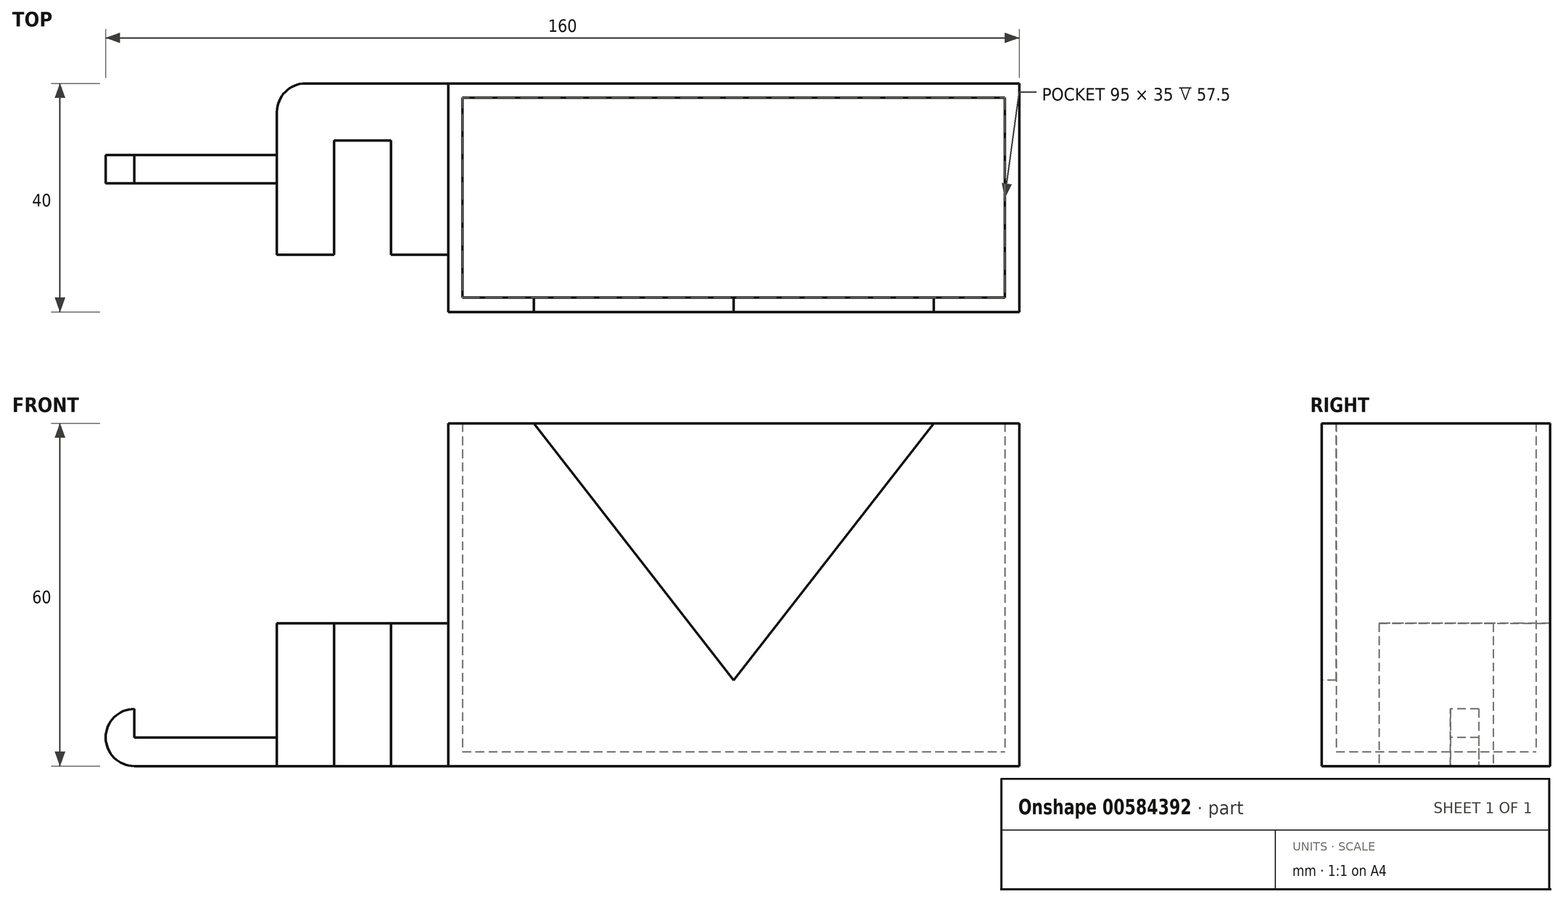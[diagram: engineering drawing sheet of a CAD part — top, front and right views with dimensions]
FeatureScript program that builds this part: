
annotation { "Feature Type Name" : "Feature", "Feature Type Description" : "" }
export const myFeature = defineFeature(function(context is Context, id is Id, definition is map)
    precondition{}
    {
        {
            var Q0;
            Q0=qCreatedBy(makeId("Top.planeOp"),FACE);
            var sketch = newSketch(context, id + "F0", { "sketchPlane" : qUnion([Q0])});
            skLineSegment(sketch, "E0.bottom", {"start": v(0, 0) * mm, "end": v(100, 0) * mm});
            skLineSegment(sketch, "E0.top", {"start": v(0, 40) * mm, "end": v(100, 40) * mm});
            skLineSegment(sketch, "E0.left", {"start": v(0, 0) * mm, "end": v(0, 40) * mm});
            skLineSegment(sketch, "E0.right", {"start": v(100, 0) * mm, "end": v(100, 40) * mm});
            skLineSegment(sketch, "E1", {"start": v(0, 40) * mm, "end": v(-30, 40) * mm});
            skLineSegment(sketch, "E2", {"start": v(-30, 40) * mm, "end": v(-30, 10) * mm});
            skLineSegment(sketch, "E3", {"start": v(-30, 10) * mm, "end": v(0, 10) * mm});
            skLineSegment(sketch, "E4", {"start": v(-30, 40) * mm, "end": v(-60, 40) * mm});
            skLineSegment(sketch, "E5", {"start": v(-60, 40) * mm, "end": v(-60, 10) * mm});
            skLineSegment(sketch, "E6", {"start": v(-60, 10) * mm, "end": v(-30, 10) * mm});
            skLineSegment(sketch, "E7", {"start": v(-10, 10) * mm, "end": v(-10, 30) * mm});
            skLineSegment(sketch, "E8", {"start": v(-10, 30) * mm, "end": v(-20, 30) * mm});
            skLineSegment(sketch, "E9", {"start": v(-20, 30) * mm, "end": v(-20, 10) * mm});
            skLineSegment(sketch, "E10", {"start": v(-40, 10) * mm, "end": v(-40, 30) * mm});
            skLineSegment(sketch, "E11", {"start": v(-40, 30) * mm, "end": v(-50, 30) * mm});
            skLineSegment(sketch, "E12", {"start": v(-50, 30) * mm, "end": v(-50, 10) * mm});
            skSolve(sketch);
        }
        {
            var Q0;
            Q0=makeQuery(id+"F0.imprint","IMPRINT",FACE,{"disambiguationData":[TD([[makeQuery(id+"F0.imprint","IMPRINT",EDGE,{"derivedFrom":sQuery(id+"F0.wireOp",EDGE,"E0.bottom")}),1.0]])]});
            extrude(context, id + "F1", {"entities" : qUnion([Q0]), "depth" : 60 * mm, "offsetDistance" : 25 * mm});
        }
        {
            var Q0;
            Q0=makeQuery(id+"F1.opExtrude","CAP_FACE",FACE,{"disambiguationData":[OSD([sQuery(id+"F0.wireOp",EDGE,"E0.bottom"),sQuery(id+"F0.wireOp",EDGE,"E0.top"),sQuery(id+"F0.wireOp",EDGE,"E0.right"),sQuery(id+"F0.wireOp",EDGE,"3OmhZuot-nZRl-fitB-kn2A-HAzrbiBYZeYS.left")])],"isStart":false});
            shell(context, id + "F2", {"entities" : qUnion([Q0]), "thickness" : 2.5 * mm});
        }
        {
            var Q0;
            {var subQ3=sQuery(id+"F0.wireOp",EDGE,"E1");Q0=makeQuery(id+"F0.imprint","IMPRINT",FACE,{"disambiguationData":[TD([[makeQuery(id+"F0.imprint","IMPRINT",EDGE,{"derivedFrom":subQ3}),1.0]])]});}
            extrude(context, id + "F3", {"entities" : qUnion([Q0]), "depth" : 25 * mm, "offsetDistance" : 25 * mm});
        }
        {
            var Q0;
            Q0=qCreatedBy(makeId("Top.planeOp"),FACE);
            var sketch = newSketch(context, id + "F4", { "sketchPlane" : qUnion([Q0])});
            skLineSegment(sketch, "E13.0", {"start": v(0, 40) * mm, "end": v(-30, 40) * mm});
            skLineSegment(sketch, "E13.1", {"start": v(-30, 40) * mm, "end": v(-30, 10) * mm});
            skLineSegment(sketch, "E13.2", {"start": v(-30, 10) * mm, "end": v(0, 10) * mm});
            skLineSegment(sketch, "E14.0", {"start": v(-20, 30) * mm, "end": v(-20, 10) * mm});
            skLineSegment(sketch, "E15", {"start": v(-30, 27.5) * mm, "end": v(-60, 27.5) * mm});
            skLineSegment(sketch, "E16", {"start": v(-60, 27.5) * mm, "end": v(-60, 22.5) * mm});
            skLineSegment(sketch, "E17", {"start": v(-60, 22.5) * mm, "end": v(-30, 22.5) * mm});
            skLineSegment(sketch, "E18", {"start": v(-55, 27.5) * mm, "end": v(-55, 22.5) * mm});
            skSolve(sketch);
        }
        {
            var Q0;
            {var subQ5=sQuery(id+"F4.wireOp",EDGE,"E18");Q0=makeQuery(id+"F4.imprint","IMPRINT",FACE,{"disambiguationData":[TD([[makeQuery(id+"F4.imprint","IMPRINT",EDGE,{"derivedFrom":subQ5}),1.0]])]});}
            extrude(context, id + "F5", {"entities" : qUnion([Q0]), "operationType" : NewBodyOperationType.ADD, "depth" : 5 * mm, "offsetDistance" : 25 * mm});
        }
        {
            var Q0;
            {var subQ0=sQuery(id+"F4.wireOp",EDGE,"E16");Q0=makeQuery(id+"F4.imprint","IMPRINT",FACE,{"disambiguationData":[TD([[makeQuery(id+"F4.imprint","IMPRINT",EDGE,{"derivedFrom":subQ0}),1.0]])]});}
            extrude(context, id + "F6", {"entities" : qUnion([Q0]), "operationType" : NewBodyOperationType.ADD, "depth" : 10 * mm, "offsetDistance" : 25 * mm});
        }
        {
            var Q0;
            Q0=makeQuery(id+"F5.opExtrude","CAP_EDGE",EDGE,{"disambiguationData":[OSD([sQuery(id+"F4.wireOp",EDGE,"E13.1")])],"isStart":false});
            var Q1;
            Q1=makeQuery(id+"F5.opExtrude","SWEPT_EDGE",EDGE,{"disambiguationData":[OSD([sQuery(id+"F4.wireOp",EDGE,"E13.1"),sQuery(id+"F4.wireOp",EDGE,"E17")])]});
            var Q2;
            Q2=makeQuery(id+"F5.opExtrude","SWEPT_EDGE",EDGE,{"disambiguationData":[OSD([sQuery(id+"F4.wireOp",EDGE,"E13.1"),sQuery(id+"F4.wireOp",EDGE,"E15")])]});
            var Q3;
            Q3=makeQuery(id+"F5.opExtrude","CAP_EDGE",EDGE,{"disambiguationData":[OSD([sQuery(id+"F4.wireOp",EDGE,"E18")])],"isStart":false});
            var Q4;
            Q4=makeQuery(id+"F6.opExtrude","CAP_EDGE",EDGE,{"disambiguationData":[OSD([sQuery(id+"F4.wireOp",EDGE,"E16")])],"isStart":true});
            var Q5;
            Q5=makeQuery(id+"F6.opExtrude","CAP_EDGE",EDGE,{"disambiguationData":[OSD([sQuery(id+"F4.wireOp",EDGE,"E16")])],"isStart":false});
            fillet(context, id + "F7", {"entities" : qUnion([Q0, Q1, Q2, Q3, Q4, Q5]), "radius" : 5 * mm, "tangentPropagation" : true, "allowEdgeOverflow" : false});
        }
        {
            var Q0;
            Q0=makeQuery(id+"F3.opExtrude","SWEPT_EDGE",EDGE,{"disambiguationData":[OSD([sQuery(id+"F0.wireOp",EDGE,"E1"),sQuery(id+"F0.wireOp",EDGE,"E2"),sQuery(id+"F0.wireOp",EDGE,"E4")])]});
            fillet(context, id + "F8", {"entities" : qUnion([Q0]), "radius" : 5 * mm, "tangentPropagation" : true, "allowEdgeOverflow" : false});
        }
        {
            var Q0;
            Q0=makeQuery(id+"F1.opExtrude","SWEPT_FACE",FACE,{"disambiguationData":[OSD([sQuery(id+"F0.wireOp",EDGE,"E0.bottom")])]});
            var sketch = newSketch(context, id + "F9", { "sketchPlane" : qUnion([Q0])});
            skLineSegment(sketch, "E19.0", {"start": v(0, 60) * mm, "end": v(100, 60) * mm});
            skLineSegment(sketch, "E19.1", {"start": v(100, 60) * mm, "end": v(100, 0) * mm});
            skLineSegment(sketch, "E19.2", {"start": v(0, 0) * mm, "end": v(100, 0) * mm});
            skLineSegment(sketch, "E19.3", {"start": v(0, 60) * mm, "end": v(0, 0) * mm});
            skLineSegment(sketch, "E20", {"start": v(50, 0) * mm, "end": v(50, 15) * mm, "construction": true});
            skLineSegment(sketch, "E21", {"start": v(0, 60) * mm, "end": v(15, 60) * mm, "construction": true});
            skLineSegment(sketch, "E22", {"start": v(100, 60) * mm, "end": v(85, 60) * mm, "construction": true});
            skLineSegment(sketch, "E23", {"start": v(15, 60) * mm, "end": v(50, 15) * mm});
            skLineSegment(sketch, "E24", {"start": v(85, 60) * mm, "end": v(50, 15) * mm});
            skSolve(sketch);
        }
        {
            var Q0;
            {var subQ0=sQuery(id+"F9.wireOp",EDGE,"E23");Q0=makeQuery(id+"F9.imprint","IMPRINT",FACE,{"disambiguationData":[TD([[makeQuery(id+"F9.imprint","IMPRINT",EDGE,{"derivedFrom":subQ0}),1.0]])]});}
            extrude(context, id + "F10", {"entities" : qUnion([Q0]), "operationType" : NewBodyOperationType.REMOVE, "oppositeDirection" : true, "depth" : 25 * mm, "offsetDistance" : 25 * mm});
        }
    });
